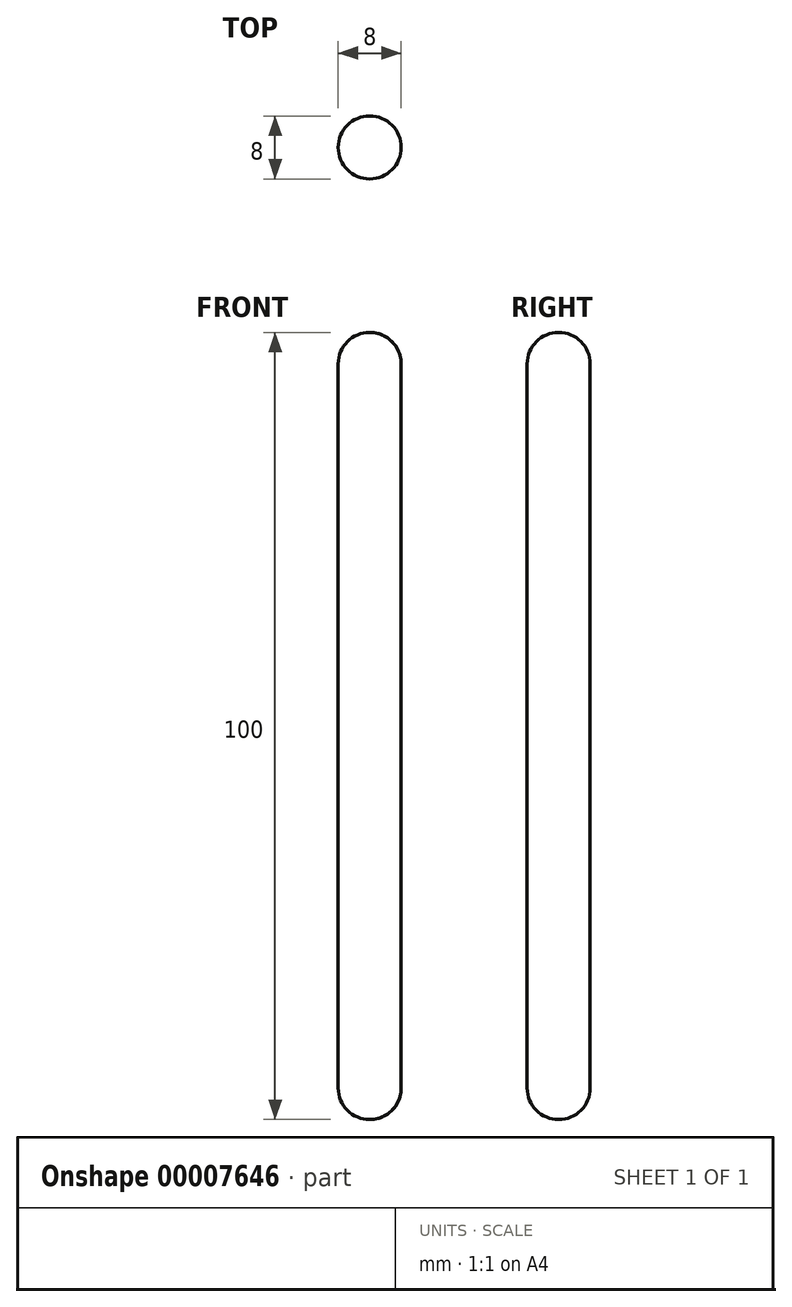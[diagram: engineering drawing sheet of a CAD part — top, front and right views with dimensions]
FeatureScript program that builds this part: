
annotation { "Feature Type Name" : "Feature", "Feature Type Description" : "" }
export const myFeature = defineFeature(function(context is Context, id is Id, definition is map)
    precondition{}
    {
        {
            var Q0;
            Q0=qCreatedBy(makeId("Top.planeOp"),FACE);
            var sketch = newSketch(context, id + "F0", { "sketchPlane" : qUnion([Q0])});
            skCircle(sketch, "E0", {"center": v(0, 0) * mm, "radius": 4 * mm});
            skSolve(sketch);
        }
        {
            var Q0;
            Q0 = qSketchRegion(id + "F0", true);
            extrude(context, id + "F1", {"entities" : qUnion([Q0]), "depth" : 100 * mm, "symmetric" : true});
        }
        {
            var Q0;
            Q0=makeQuery(id+"F1.opExtrude","CAP_EDGE",EDGE,{"disambiguationData":[OSD([sQuery(id+"F0.wireOp",EDGE,"E0")])],"isStart":false});
            var Q1;
            Q1=makeQuery(id+"F1.opExtrude","CAP_EDGE",EDGE,{"disambiguationData":[OSD([sQuery(id+"F0.wireOp",EDGE,"E0")])],"isStart":true});
            fillet(context, id + "F2", {"entities" : qUnion([Q0, Q1]), "radius" : 4 * mm, "tangentPropagation" : true, "allowEdgeOverflow" : false});
        }
    });
